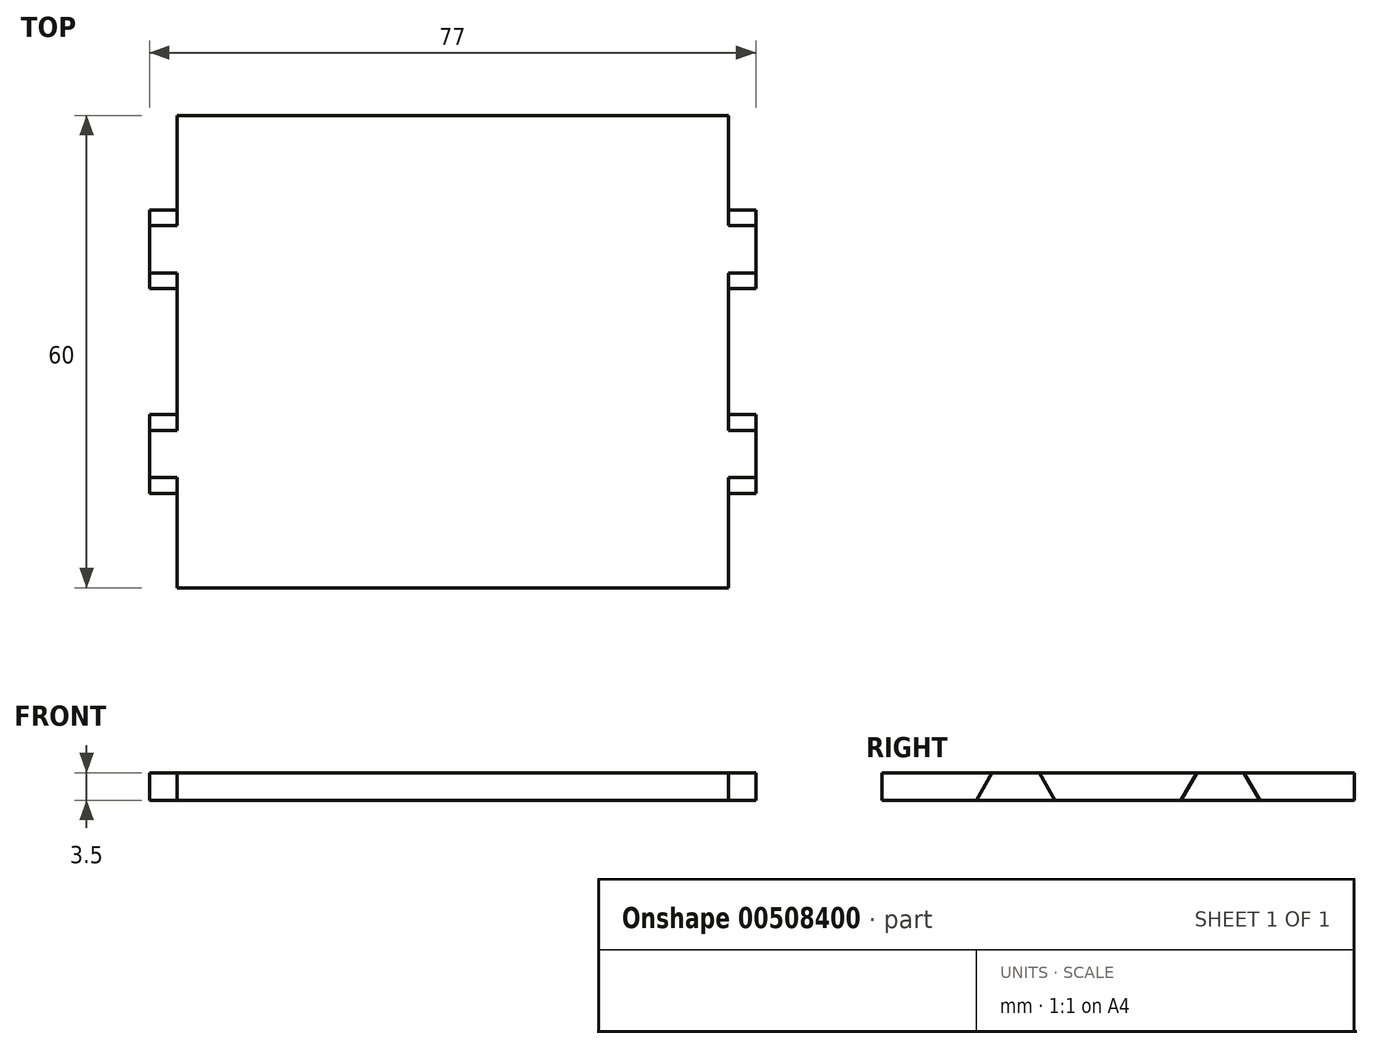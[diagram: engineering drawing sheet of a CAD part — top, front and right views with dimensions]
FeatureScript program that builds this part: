
annotation { "Feature Type Name" : "Feature", "Feature Type Description" : "" }
export const myFeature = defineFeature(function(context is Context, id is Id, definition is map)
    precondition{}
    {
        {
            var Q0;
            Q0=qCreatedBy(makeId("Top.planeOp"),FACE);
            var sketch = newSketch(context, id + "F0", { "sketchPlane" : qUnion([Q0])});
            skLineSegment(sketch, "E0", {"start": v(-38.5, 30) * mm, "end": v(38.5, 30) * mm});
            skLineSegment(sketch, "E1", {"start": v(38.5, 30) * mm, "end": v(38.5, -30) * mm});
            skLineSegment(sketch, "E2", {"start": v(38.5, -30) * mm, "end": v(-38.5, -30) * mm});
            skLineSegment(sketch, "E3", {"start": v(-38.5, -30) * mm, "end": v(-38.5, 30) * mm});
            skSolve(sketch);
        }
        {
            var Q0;
            Q0=makeQuery(id+"F0.imprint","IMPRINT",FACE,{"disambiguationData":[TD([[makeQuery(id+"F0.imprint","IMPRINT",EDGE,{"derivedFrom":sQuery(id+"F0.wireOp",EDGE,"E0")}),-1.0]])]});
            extrude(context, id + "F1", {"entities" : qUnion([Q0]), "depth" : 3.5 * mm, "offsetDistance" : 25 * mm});
        }
        {
            var Q0;
            Q0=makeQuery(id+"F1.opExtrude","SWEPT_FACE",FACE,{"disambiguationData":[OSD([sQuery(id+"F0.wireOp",EDGE,"E3")])]});
            var sketch = newSketch(context, id + "F2", { "sketchPlane" : qUnion([Q0])});
            skLineSegment(sketch, "E4", {"start": v(-30, 3.5) * mm, "end": v(-16, 3.5) * mm});
            skLineSegment(sketch, "E5", {"start": v(-16, 3.5) * mm, "end": v(-10, 3.5) * mm});
            skLineSegment(sketch, "E6", {"start": v(-10, 3.5) * mm, "end": v(10, 3.5) * mm});
            skLineSegment(sketch, "E7", {"start": v(10, 3.5) * mm, "end": v(16, 3.5) * mm});
            skLineSegment(sketch, "E8", {"start": v(16, 3.5) * mm, "end": v(30, 3.5) * mm});
            skLineSegment(sketch, "E9", {"start": v(30, 3.5) * mm, "end": v(30, 0) * mm});
            skLineSegment(sketch, "E10", {"start": v(30, 0) * mm, "end": v(18, 0) * mm});
            skLineSegment(sketch, "E11", {"start": v(18, 0) * mm, "end": v(8, 0) * mm});
            skLineSegment(sketch, "E12", {"start": v(8, 0) * mm, "end": v(-8, 0) * mm});
            skLineSegment(sketch, "E13", {"start": v(-8, 0) * mm, "end": v(-18, 0) * mm});
            skLineSegment(sketch, "E14", {"start": v(-18, 0) * mm, "end": v(-30, 0) * mm});
            skLineSegment(sketch, "E15", {"start": v(-30, 0) * mm, "end": v(-30, 3.5) * mm});
            skLineSegment(sketch, "E16", {"start": v(-18, 0) * mm, "end": v(-16, 3.5) * mm});
            skLineSegment(sketch, "E17", {"start": v(-10, 3.5) * mm, "end": v(-8, 0) * mm});
            skLineSegment(sketch, "E18", {"start": v(8, 0) * mm, "end": v(10, 3.5) * mm});
            skLineSegment(sketch, "E19", {"start": v(16, 3.5) * mm, "end": v(18, 0) * mm});
            skSolve(sketch);
        }
        {
            var Q0;
            Q0=makeQuery(id+"F2.imprint","IMPRINT",FACE,{"disambiguationData":[TD([[makeQuery(id+"F2.imprint","IMPRINT",EDGE,{"derivedFrom":sQuery(id+"F2.wireOp",EDGE,"E4")}),1.0]])]});
            var Q1;
            Q1=makeQuery(id+"F2.imprint","IMPRINT",FACE,{"disambiguationData":[TD([[makeQuery(id+"F2.imprint","IMPRINT",EDGE,{"derivedFrom":sQuery(id+"F2.wireOp",EDGE,"E6")}),1.0]])]});
            var Q2;
            Q2=makeQuery(id+"F2.imprint","IMPRINT",FACE,{"disambiguationData":[TD([[makeQuery(id+"F2.imprint","IMPRINT",EDGE,{"derivedFrom":sQuery(id+"F2.wireOp",EDGE,"E8")}),1.0]])]});
            extrude(context, id + "F3", {"entities" : qUnion([Q0, Q1, Q2]), "operationType" : NewBodyOperationType.REMOVE, "oppositeDirection" : true, "depth" : 3.5 * mm, "offsetDistance" : 25 * mm});
        }
        {
            var Q0;
            Q0=makeQuery(id+"F1.opExtrude","SWEPT_FACE",FACE,{"disambiguationData":[OSD([sQuery(id+"F0.wireOp",EDGE,"E1")])]});
            var sketch = newSketch(context, id + "F4", { "sketchPlane" : qUnion([Q0])});
            skLineSegment(sketch, "E20", {"start": v(30, 3.5) * mm, "end": v(16, 3.5) * mm});
            skLineSegment(sketch, "E21", {"start": v(16, 3.5) * mm, "end": v(10, 3.5) * mm});
            skLineSegment(sketch, "E22", {"start": v(10, 3.5) * mm, "end": v(-10, 3.5) * mm});
            skLineSegment(sketch, "E23", {"start": v(-10, 3.5) * mm, "end": v(-16, 3.5) * mm});
            skLineSegment(sketch, "E24", {"start": v(-16, 3.5) * mm, "end": v(-30, 3.5) * mm});
            skLineSegment(sketch, "E25", {"start": v(-30, 3.5) * mm, "end": v(-30, 0) * mm});
            skLineSegment(sketch, "E26", {"start": v(-30, 0) * mm, "end": v(-18, 0) * mm});
            skLineSegment(sketch, "E27", {"start": v(-18, 0) * mm, "end": v(-8, 0) * mm});
            skLineSegment(sketch, "E28", {"start": v(-8, 0) * mm, "end": v(8, 0) * mm});
            skLineSegment(sketch, "E29", {"start": v(8, 0) * mm, "end": v(18, 0) * mm});
            skLineSegment(sketch, "E30", {"start": v(18, 0) * mm, "end": v(30, 0) * mm});
            skLineSegment(sketch, "E31", {"start": v(30, 0) * mm, "end": v(30, 3.5) * mm});
            skLineSegment(sketch, "E32", {"start": v(18, 0) * mm, "end": v(16, 3.5) * mm});
            skLineSegment(sketch, "E33", {"start": v(10, 3.5) * mm, "end": v(8, 0) * mm});
            skLineSegment(sketch, "E34", {"start": v(-8, 0) * mm, "end": v(-10, 3.5) * mm});
            skLineSegment(sketch, "E35", {"start": v(-16, 3.5) * mm, "end": v(-18, 0) * mm});
            skSolve(sketch);
        }
        {
            var Q0;
            Q0=makeQuery(id+"F4.imprint","IMPRINT",FACE,{"disambiguationData":[TD([[makeQuery(id+"F4.imprint","IMPRINT",EDGE,{"derivedFrom":sQuery(id+"F4.wireOp",EDGE,"E24")}),1.0]])]});
            var Q1;
            Q1=makeQuery(id+"F4.imprint","IMPRINT",FACE,{"disambiguationData":[TD([[makeQuery(id+"F4.imprint","IMPRINT",EDGE,{"derivedFrom":sQuery(id+"F4.wireOp",EDGE,"E22")}),1.0]])]});
            var Q2;
            Q2=makeQuery(id+"F4.imprint","IMPRINT",FACE,{"disambiguationData":[TD([[makeQuery(id+"F4.imprint","IMPRINT",EDGE,{"derivedFrom":sQuery(id+"F4.wireOp",EDGE,"E20")}),1.0]])]});
            extrude(context, id + "F5", {"entities" : qUnion([Q0, Q1, Q2]), "operationType" : NewBodyOperationType.REMOVE, "oppositeDirection" : true, "depth" : 3.5 * mm, "offsetDistance" : 25 * mm});
        }
    });
